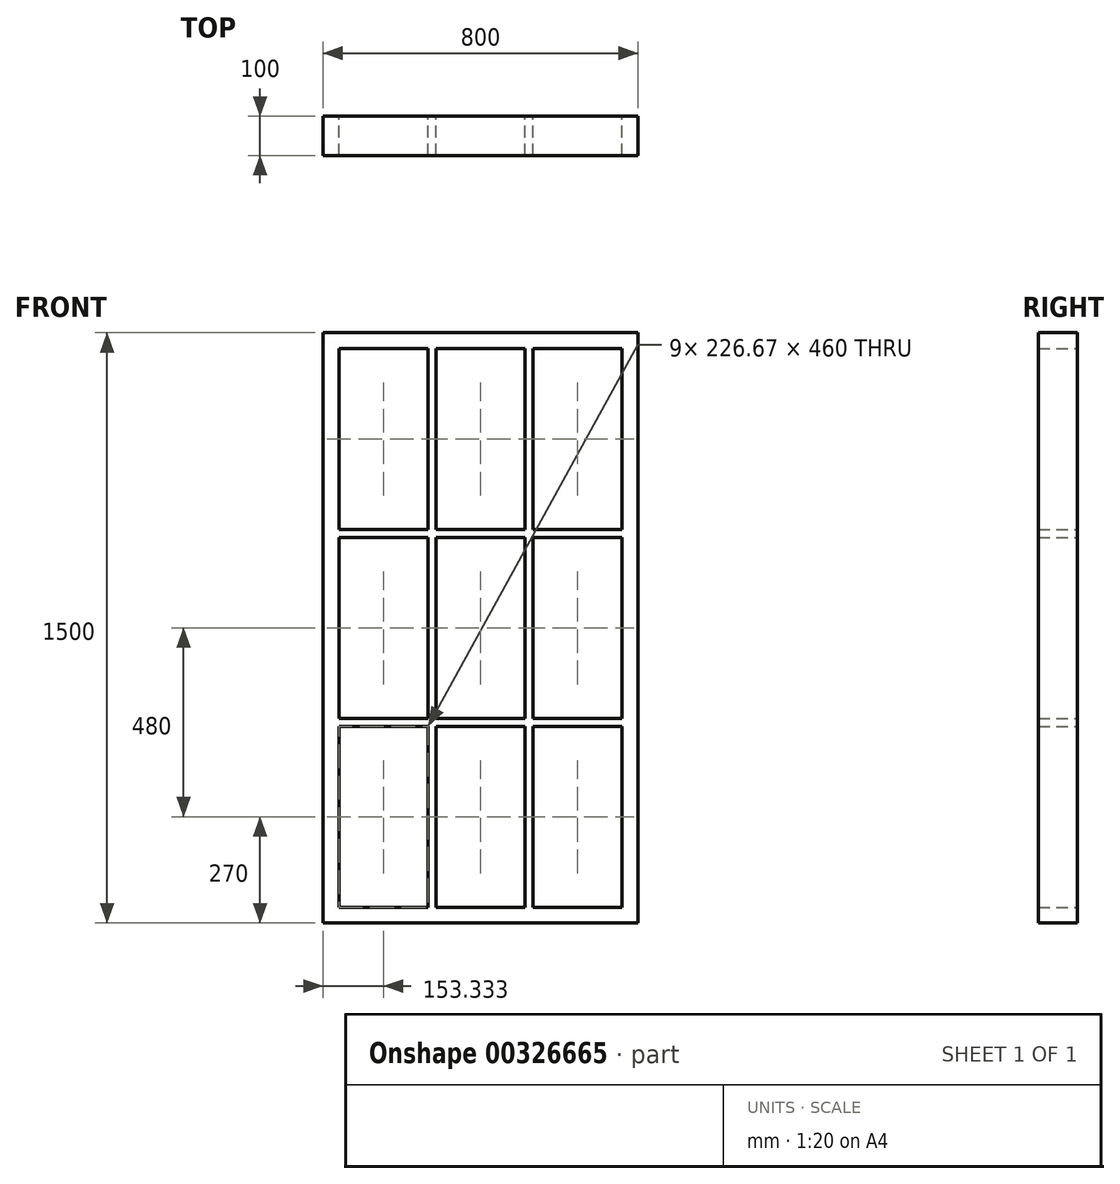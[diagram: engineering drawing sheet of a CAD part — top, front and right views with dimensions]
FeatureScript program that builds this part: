
annotation { "Feature Type Name" : "Feature", "Feature Type Description" : "" }
export const myFeature = defineFeature(function(context is Context, id is Id, definition is map)
    precondition{}
    {
        {
            var Q0;
            Q0=qCreatedBy(makeId("Front.planeOp"),FACE);
            var sketch = newSketch(context, id + "F0", { "sketchPlane" : qUnion([Q0])});
            skLineSegment(sketch, "E0.bottom", {"start": v(0, 0) * mm, "end": v(-800, 0) * mm});
            skLineSegment(sketch, "E0.top", {"start": v(0, 1500) * mm, "end": v(-800, 1500) * mm});
            skLineSegment(sketch, "E0.left", {"start": v(0, 0) * mm, "end": v(0, 1500) * mm});
            skLineSegment(sketch, "E0.right", {"start": v(-800, 0) * mm, "end": v(-800, 1500) * mm});
            skLineSegment(sketch, "E1", {"start": v(-533.33, 1460) * mm, "end": v(-533.33, 1000) * mm});
            skLineSegment(sketch, "E2", {"start": v(-513.33, 1460) * mm, "end": v(-513.33, 1000) * mm});
            skLineSegment(sketch, "E3", {"start": v(-286.67, 1460) * mm, "end": v(-286.67, 1000) * mm});
            skLineSegment(sketch, "E4", {"start": v(-266.67, 1460) * mm, "end": v(-266.67, 1000) * mm});
            skLineSegment(sketch, "E5", {"start": v(-760, 1000) * mm, "end": v(-533.33, 1000) * mm});
            skLineSegment(sketch, "E6", {"start": v(-760, 980) * mm, "end": v(-533.33, 980) * mm});
            skLineSegment(sketch, "E7", {"start": v(-760, 520) * mm, "end": v(-533.33, 520) * mm});
            skLineSegment(sketch, "E8", {"start": v(-760, 500) * mm, "end": v(-533.33, 500) * mm});
            skLineSegment(sketch, "E9.bottom", {"start": v(-760, 1460) * mm, "end": v(-533.33, 1460) * mm});
            skLineSegment(sketch, "E9.top", {"start": v(-760, 40) * mm, "end": v(-40, 40) * mm});
            skLineSegment(sketch, "E9.left", {"start": v(-760, 1460) * mm, "end": v(-760, 1000) * mm});
            skLineSegment(sketch, "E9.right", {"start": v(-40, 1460) * mm, "end": v(-40, 1000) * mm});
            skLineSegment(sketch, "E10.trimOffspring", {"start": v(-266.67, 500) * mm, "end": v(-40, 500) * mm});
            skLineSegment(sketch, "E11.trimOffspring", {"start": v(-266.67, 520) * mm, "end": v(-40, 520) * mm});
            skLineSegment(sketch, "E12.trimOffspring", {"start": v(-513.33, 500) * mm, "end": v(-286.67, 500) * mm});
            skLineSegment(sketch, "E13.trimOffspring", {"start": v(-513.33, 520) * mm, "end": v(-286.67, 520) * mm});
            skLineSegment(sketch, "E14.trimOffspring", {"start": v(-513.33, 1000) * mm, "end": v(-286.67, 1000) * mm});
            skLineSegment(sketch, "E15.trimOffspring", {"start": v(-513.33, 980) * mm, "end": v(-286.67, 980) * mm});
            skLineSegment(sketch, "E16.trimOffspring", {"start": v(-266.67, 1000) * mm, "end": v(-40, 1000) * mm});
            skLineSegment(sketch, "E17.trimOffspring", {"start": v(-266.67, 980) * mm, "end": v(-40, 980) * mm});
            skLineSegment(sketch, "E18.trimOffspring", {"start": v(-40, 980) * mm, "end": v(-40, 520) * mm});
            skLineSegment(sketch, "E19.trimOffspring", {"start": v(-533.33, 980) * mm, "end": v(-533.33, 520) * mm});
            skLineSegment(sketch, "E20.trimOffspring", {"start": v(-513.33, 980) * mm, "end": v(-513.33, 520) * mm});
            skLineSegment(sketch, "E21.trimOffspring", {"start": v(-513.33, 500) * mm, "end": v(-513.33, 40) * mm});
            skLineSegment(sketch, "E22.trimOffspring", {"start": v(-533.33, 500) * mm, "end": v(-533.33, 40) * mm});
            skLineSegment(sketch, "E23.trimOffspring", {"start": v(-266.67, 500) * mm, "end": v(-266.67, 40) * mm});
            skLineSegment(sketch, "E24.trimOffspring", {"start": v(-286.67, 500) * mm, "end": v(-286.67, 40) * mm});
            skLineSegment(sketch, "E25.trimOffspring", {"start": v(-760, 500) * mm, "end": v(-760, 40) * mm});
            skLineSegment(sketch, "E26.trimOffspring", {"start": v(-40, 500) * mm, "end": v(-40, 40) * mm});
            skLineSegment(sketch, "E27.trimOffspring", {"start": v(-760, 980) * mm, "end": v(-760, 520) * mm});
            skLineSegment(sketch, "E28.trimOffspring", {"start": v(-266.67, 1460) * mm, "end": v(-40, 1460) * mm});
            skLineSegment(sketch, "E29.trimOffspring", {"start": v(-513.33, 1460) * mm, "end": v(-286.67, 1460) * mm});
            skLineSegment(sketch, "E30.trimOffspring", {"start": v(-266.67, 980) * mm, "end": v(-266.67, 520) * mm});
            skLineSegment(sketch, "E31.trimOffspring", {"start": v(-286.67, 980) * mm, "end": v(-286.67, 520) * mm});
            skSolve(sketch);
        }
        {
            var Q0;
            Q0 = qSketchRegion(id + "F0", true);
            extrude(context, id + "F1", {"entities" : qUnion([Q0]), "depth" : 100 * mm});
        }
    });
